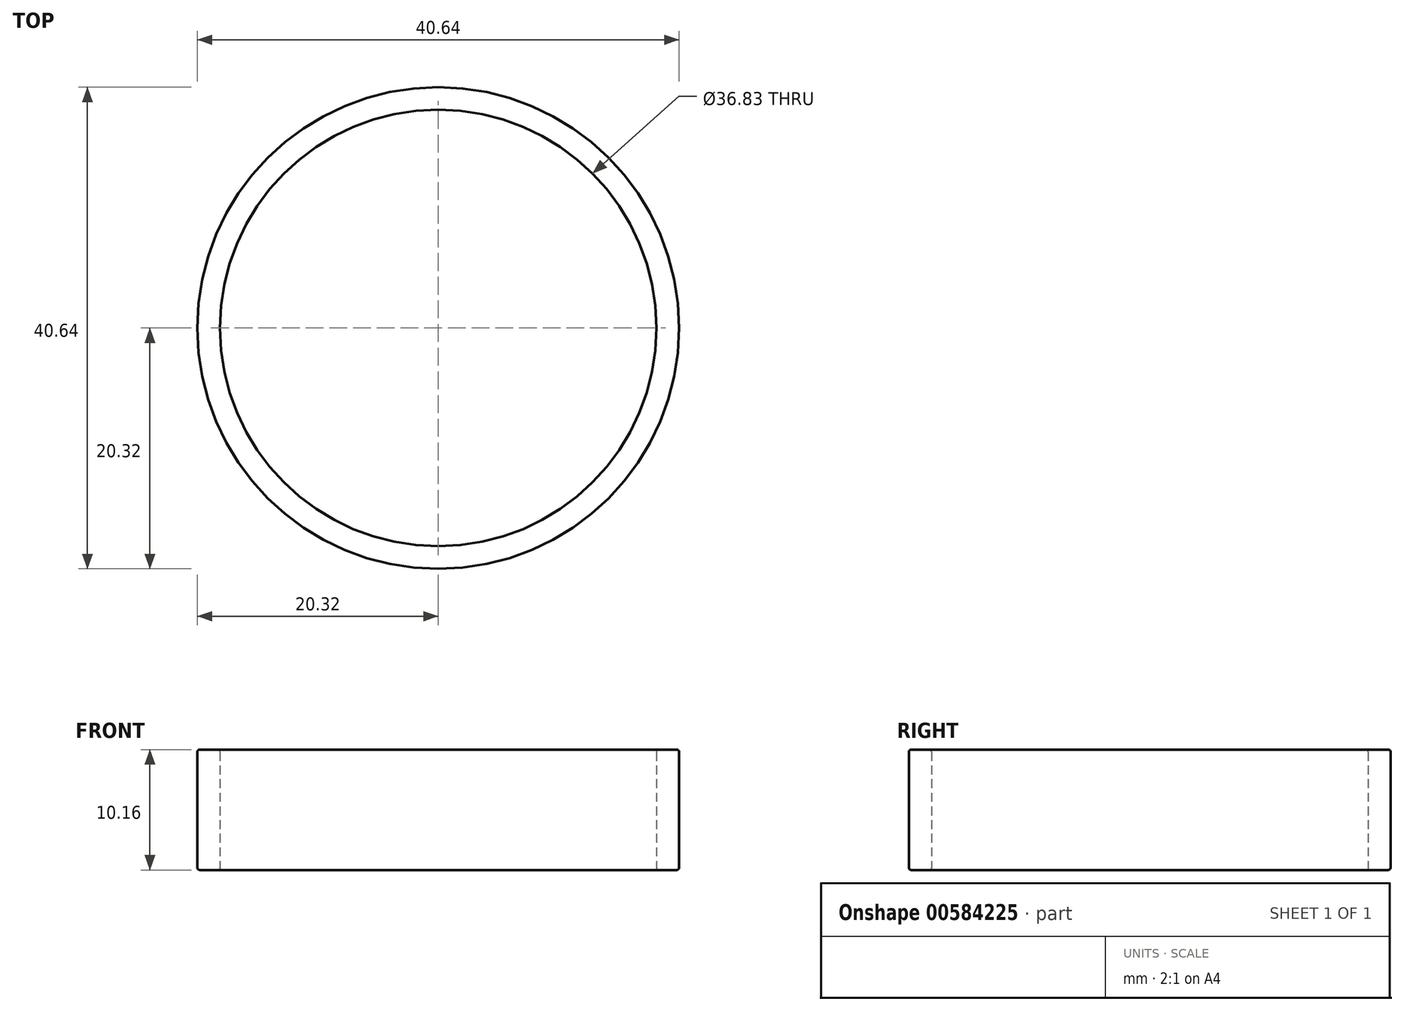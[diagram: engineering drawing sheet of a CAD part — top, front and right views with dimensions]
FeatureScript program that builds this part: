
annotation { "Feature Type Name" : "Feature", "Feature Type Description" : "" }
export const myFeature = defineFeature(function(context is Context, id is Id, definition is map)
    precondition{}
    {
        {
            var Q0;
            Q0=qCreatedBy(makeId("Top.planeOp"),FACE);
            var sketch = newSketch(context, id + "F0", { "sketchPlane" : qUnion([Q0])});
            skCircle(sketch, "E0", {"center": v(0, 0) * mm, "radius": 20.32 * mm});
            skSolve(sketch);
        }
        {
            var Q0;
            Q0 = qSketchRegion(id + "F0", true);
            extrude(context, id + "F1", {"entities" : qUnion([Q0]), "depth" : 10.16 * mm, "offsetDistance" : 25.4 * mm});
        }
        {
            var Q0;
            Q0=qCreatedBy(makeId("Top.planeOp"),FACE);
            var sketch = newSketch(context, id + "F2", { "sketchPlane" : qUnion([Q0])});
            skCircle(sketch, "E1", {"center": v(0, 0) * mm, "radius": 18.41 * mm});
            skSolve(sketch);
        }
        {
            var Q0;
            Q0 = qSketchRegion(id + "F2", true);
            extrude(context, id + "F3", {"entities" : qUnion([Q0]), "operationType" : NewBodyOperationType.REMOVE, "endBound" : BoundingType.SYMMETRIC, "depth" : 25.4 * mm, "offsetDistance" : 25.4 * mm});
        }
        {
            var Q0;
            Q0=makeQuery(id+"F1.opExtrude","CAP_EDGE",EDGE,{"disambiguationData":[OSD([sQuery(id+"F0.wireOp",EDGE,"E0")])],"isStart":false});
            var Q1;
            Q1=makeQuery(id+"F3.boolean.opBoolean","INTERSECT",EDGE,{"derivedFrom":[makeQuery(id+"F1.opExtrude","CAP_FACE",FACE,{"disambiguationData":[OSD([sQuery(id+"F0.wireOp",EDGE,"E0")])],"isStart":false}),makeQuery(id+"F3.opExtrude","SWEPT_FACE",FACE,{"disambiguationData":[OSD([sQuery(id+"F2.wireOp",EDGE,"E1")])]})]});
            var Q2;
            Q2=makeQuery(id+"F1.opExtrude","CAP_EDGE",EDGE,{"disambiguationData":[OSD([sQuery(id+"F0.wireOp",EDGE,"E0")])],"isStart":true});
            var Q3;
            Q3=makeQuery(id+"F3.boolean.opBoolean","INTERSECT",EDGE,{"derivedFrom":[makeQuery(id+"F1.opExtrude","CAP_FACE",FACE,{"disambiguationData":[OSD([sQuery(id+"F0.wireOp",EDGE,"E0")])],"isStart":true}),makeQuery(id+"F3.opExtrude","SWEPT_FACE",FACE,{"disambiguationData":[OSD([sQuery(id+"F2.wireOp",EDGE,"E1")])]})]});
            fillet(context, id + "F4", {"entities" : qUnion([Q0, Q1, Q2, Q3]), "radius" : 0.2 * mm, "tangentPropagation" : true, "allowEdgeOverflow" : false});
        }
    });
